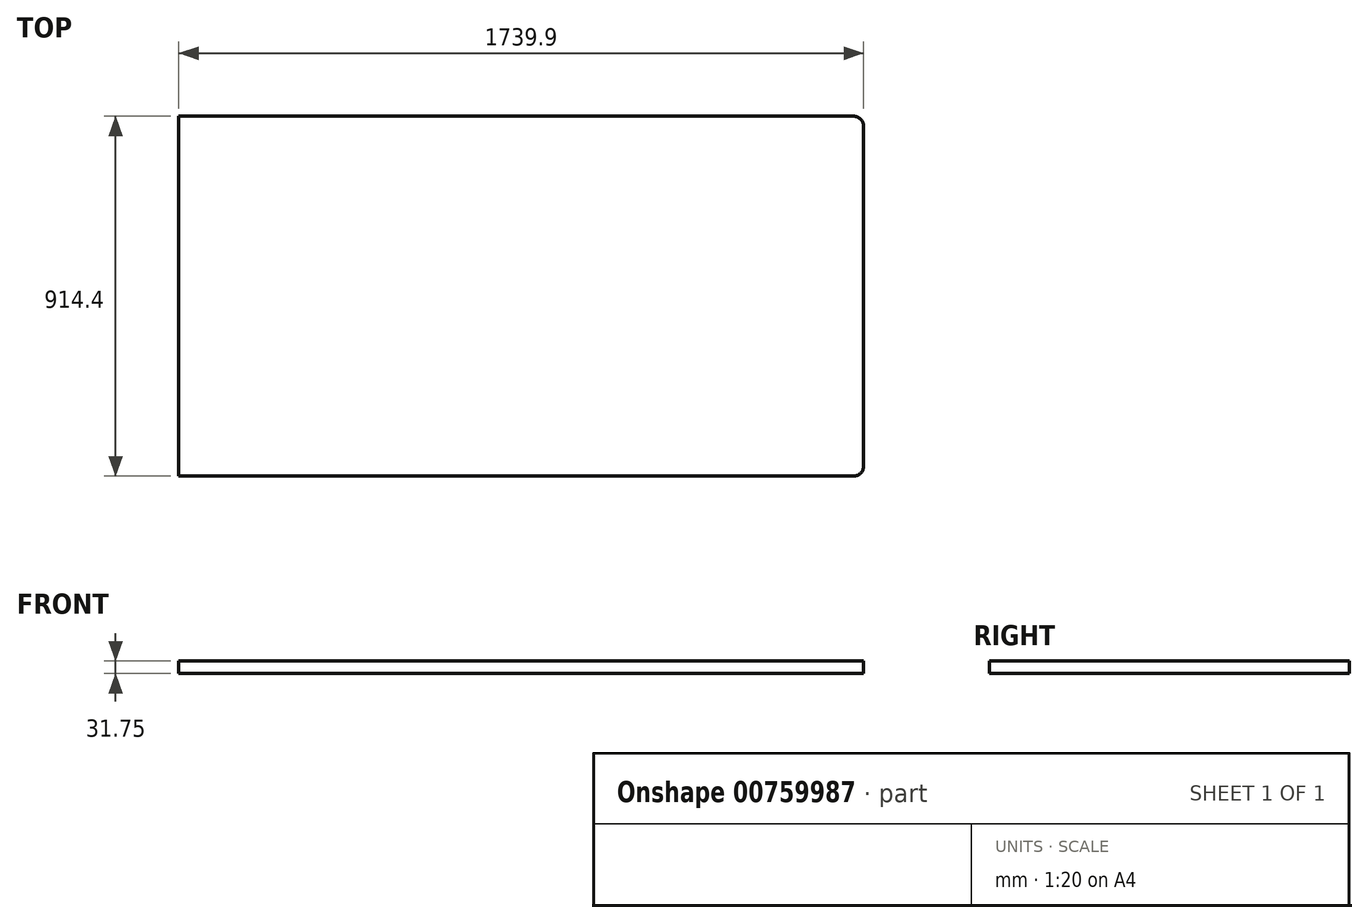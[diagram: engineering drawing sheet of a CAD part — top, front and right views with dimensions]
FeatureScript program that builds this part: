
annotation { "Feature Type Name" : "Feature", "Feature Type Description" : "" }
export const myFeature = defineFeature(function(context is Context, id is Id, definition is map)
    precondition{}
    {
        {
            var Q0;
            Q0=qCreatedBy(makeId("Top.planeOp"),FACE);
            var sketch = newSketch(context, id + "F0", { "sketchPlane" : qUnion([Q0])});
            skLineSegment(sketch, "E0.bottom", {"start": v(0, 0) * mm, "end": v(1739.9, 0) * mm});
            skLineSegment(sketch, "E0.top", {"start": v(0, 914.4) * mm, "end": v(1739.9, 914.4) * mm});
            skLineSegment(sketch, "E0.left", {"start": v(0, 0) * mm, "end": v(0, 914.4) * mm});
            skLineSegment(sketch, "E0.right", {"start": v(1739.9, 0) * mm, "end": v(1739.9, 914.4) * mm});
            skSolve(sketch);
        }
        {
            var Q0;
            Q0=makeQuery(id+"F0.imprint","IMPRINT",FACE,{"disambiguationData":[TD([[makeQuery(id+"F0.imprint","IMPRINT",EDGE,{"derivedFrom":sQuery(id+"F0.wireOp",EDGE,"E0.bottom")}),1.0]])]});
            extrude(context, id + "F1", {"entities" : qUnion([Q0]), "oppositeDirection" : true, "depth" : 31.75 * mm, "offsetDistance" : 25.4 * mm});
        }
        {
            var Q0;
            Q0=makeQuery(id+"F1.opExtrude","SWEPT_EDGE",EDGE,{"disambiguationData":[OSD([sQuery(id+"F0.wireOp",EDGE,"E0.bottom"),sQuery(id+"F0.wireOp",EDGE,"E0.right")])]});
            var Q1;
            Q1=makeQuery(id+"F1.opExtrude","SWEPT_EDGE",EDGE,{"disambiguationData":[OSD([sQuery(id+"F0.wireOp",EDGE,"E0.top"),sQuery(id+"F0.wireOp",EDGE,"E0.right")])]});
            fillet(context, id + "F2", {"entities" : qUnion([Q0, Q1]), "radius" : 25.4 * mm, "tangentPropagation" : true, "allowEdgeOverflow" : false});
        }
    });
